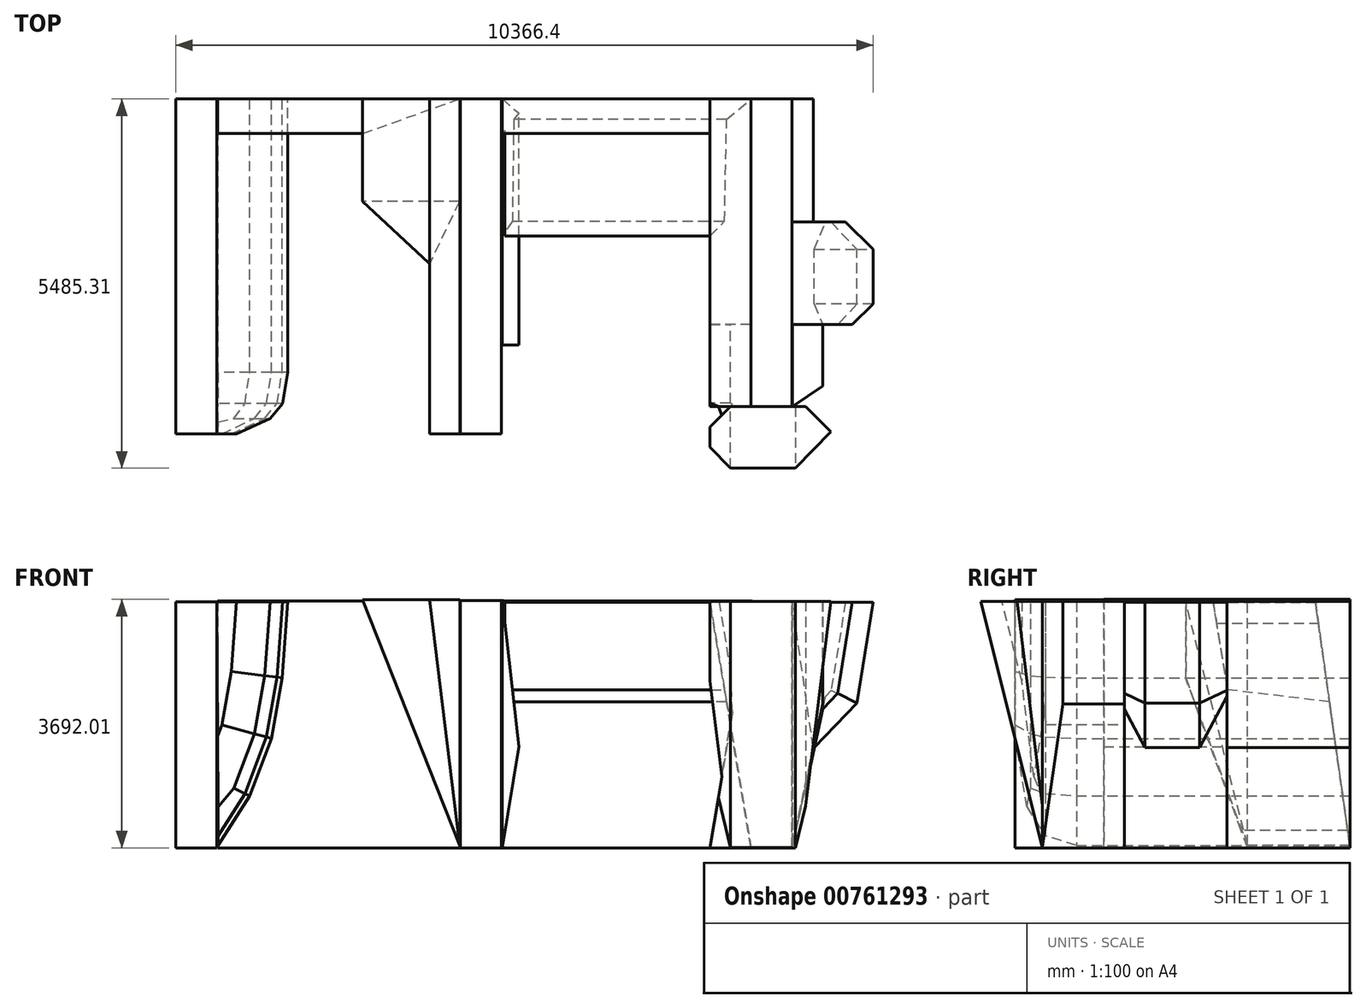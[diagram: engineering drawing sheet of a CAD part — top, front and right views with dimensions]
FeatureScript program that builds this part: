
annotation { "Feature Type Name" : "Feature", "Feature Type Description" : "" }
export const myFeature = defineFeature(function(context is Context, id is Id, definition is map)
    precondition{}
    {
        {
            var Q0;
            Q0=qCreatedBy(makeId("Front.planeOp"),FACE);
            var sketch = newSketch(context, id + "F0", { "sketchPlane" : qUnion([Q0])});
            skLineSegment(sketch, "E0.bottom", {"start": v(0, 0) * mm, "end": v(609.6, 0) * mm});
            skLineSegment(sketch, "E0.top", {"start": v(0, 3657.6) * mm, "end": v(609.6, 3657.6) * mm});
            skLineSegment(sketch, "E0.left", {"start": v(0, 0) * mm, "end": v(0, 3657.6) * mm});
            skLineSegment(sketch, "E0.right", {"start": v(609.6, 0) * mm, "end": v(609.6, 3657.6) * mm});
            skSolve(sketch);
        }
        {
            var Q0;
            Q0 = qSketchRegion(id + "F0", true);
            extrude(context, id + "F1", {"entities" : qUnion([Q0]), "depth" : 4572 * mm, "offsetDistance" : 25.4 * mm});
        }
        {
            var Q0;
            Q0=qCreatedBy(makeId("Front.planeOp"),FACE);
            var sketch = newSketch(context, id + "F2", { "sketchPlane" : qUnion([Q0])});
            skLineSegment(sketch, "E1", {"start": v(612.05, 0) * mm, "end": v(1069.66, 2135.93) * mm});
            skLineSegment(sketch, "E2", {"start": v(1069.66, 2135.93) * mm, "end": v(1069.66, 3659.93) * mm});
            skLineSegment(sketch, "E3", {"start": v(1069.66, 3659.93) * mm, "end": v(618.62, 3659.93) * mm});
            skLineSegment(sketch, "E4", {"start": v(618.62, 3659.93) * mm, "end": v(612.05, 0) * mm});
            skSolve(sketch);
        }
        {
            var Q0;
            Q0 = qSketchRegion(id + "F2", true);
            extrude(context, id + "F3", {"entities" : qUnion([Q0]), "depth" : 4572 * mm, "offsetDistance" : 25.4 * mm, "hasSecondDirection" : true, "secondDirectionOppositeDirection" : false, "secondDirectionDepth" : 3352.8 * mm});
        }
        {
            var Q0;
            Q0=makeQuery(id+"F3.opExtrude","CAP_EDGE",EDGE,{"disambiguationData":[OSD([sQuery(id+"F2.wireOp",EDGE,"E2")])],"isStart":false});
            chamfer(context, id + "F4", {"entities" : qUnion([Q0]), "chamferType" : ChamferType.TWO_OFFSETS, "width1" : 457.2 * mm, "oppositeDirection" : false, "width2" : 304.8 * mm, "tangentPropagation" : true});
        }
        {
            var Q0;
            Q0=qCreatedBy(makeId("Front.planeOp"),FACE);
            var sketch = newSketch(context, id + "F5", { "sketchPlane" : qUnion([Q0])});
            skLineSegment(sketch, "E5", {"start": v(618.5, 0) * mm, "end": v(942.34, 1489.2) * mm});
            skLineSegment(sketch, "E6", {"start": v(942.34, 1489.2) * mm, "end": v(1573.15, 2151.17) * mm});
            skLineSegment(sketch, "E7", {"start": v(1573.15, 2151.17) * mm, "end": v(1816.44, 3651.3) * mm});
            skLineSegment(sketch, "E8", {"start": v(1816.44, 3651.3) * mm, "end": v(1054.44, 3651.3) * mm});
            skLineSegment(sketch, "E9", {"start": v(1054.44, 3651.3) * mm, "end": v(611.92, 3651.3) * mm});
            skLineSegment(sketch, "E10", {"start": v(611.92, 3651.3) * mm, "end": v(618.5, 0) * mm});
            skSolve(sketch);
        }
        {
            var Q0;
            Q0 = qSketchRegion(id + "F5", true);
            extrude(context, id + "F6", {"entities" : qUnion([Q0]), "operationType" : NewBodyOperationType.ADD, "depth" : 3352.8 * mm, "offsetDistance" : 25.4 * mm, "hasSecondDirection" : true, "secondDirectionOppositeDirection" : true, "secondDirectionDepth" : -1828.8 * mm});
        }
        {
            var Q0;
            Q0=makeQuery(id+"F6.opExtrude","CAP_EDGE",EDGE,{"disambiguationData":[OSD([sQuery(id+"F5.wireOp",EDGE,"E7")])],"isStart":false});
            var Q1;
            Q1=makeQuery(id+"F6.opExtrude","CAP_EDGE",EDGE,{"disambiguationData":[OSD([sQuery(id+"F5.wireOp",EDGE,"E6")])],"isStart":false});
            chamfer(context, id + "F7", {"entities" : qUnion([Q0, Q1]), "width" : 304.8 * mm, "tangentPropagation" : true});
        }
        {
            var Q0;
            Q0=makeQuery(id+"F6.opExtrude","CAP_EDGE",EDGE,{"disambiguationData":[OSD([sQuery(id+"F5.wireOp",EDGE,"E7")])],"isStart":true});
            var Q1;
            Q1=makeQuery(id+"F6.opExtrude","CAP_EDGE",EDGE,{"disambiguationData":[OSD([sQuery(id+"F5.wireOp",EDGE,"E6")])],"isStart":true});
            chamfer(context, id + "F8", {"entities" : qUnion([Q0, Q1]), "width" : 406.4 * mm, "tangentPropagation" : true});
        }
        {
            var Q0;
            Q0=qCreatedBy(makeId("Front.planeOp"),FACE);
            var sketch = newSketch(context, id + "F9", { "sketchPlane" : qUnion([Q0])});
            skLineSegment(sketch, "E11", {"start": v(610.13, 0) * mm, "end": v(925.77, 1490.96) * mm});
            skLineSegment(sketch, "E12", {"start": v(925.77, 1490.96) * mm, "end": v(610.13, 3664.47) * mm});
            skLineSegment(sketch, "E13", {"start": v(610.13, 3664.47) * mm, "end": v(610.13, 0) * mm});
            skSolve(sketch);
        }
        {
            var Q0;
            Q0 = qSketchRegion(id + "F9", true);
            extrude(context, id + "F10", {"entities" : qUnion([Q0]), "operationType" : NewBodyOperationType.ADD, "depth" : 1828.8 * mm, "offsetDistance" : 25.4 * mm});
        }
        {
            var Q0;
            Q0=qCreatedBy(makeId("Right.planeOp"),FACE);
            var sketch = newSketch(context, id + "F11", { "sketchPlane" : qUnion([Q0])});
            skLineSegment(sketch, "E14", {"start": v(-4570.91, 0) * mm, "end": v(-4570.91, 3662.43) * mm});
            skLineSegment(sketch, "E15", {"start": v(-4570.91, 3662.43) * mm, "end": v(-5485.31, 3662.43) * mm});
            skLineSegment(sketch, "E16", {"start": v(-5485.31, 3662.43) * mm, "end": v(-4570.91, 0) * mm});
            skSolve(sketch);
        }
        {
            var Q0;
            Q0 = qSketchRegion(id + "F11", true);
            extrude(context, id + "F12", {"entities" : qUnion([Q0]), "operationType" : NewBodyOperationType.ADD, "depth" : 1219.2 * mm, "offsetDistance" : 25.4 * mm, "hasSecondDirection" : true, "secondDirectionOppositeDirection" : true, "secondDirectionDepth" : 609.6 * mm});
        }
        {
            var Q0;
            Q0=makeQuery(id+"F12.opExtrude","CAP_EDGE",EDGE,{"disambiguationData":[OSD([sQuery(id+"F11.wireOp",EDGE,"E16")])],"isStart":false});
            chamfer(context, id + "F13", {"entities" : qUnion([Q0]), "width" : 558.8 * mm, "tangentPropagation" : true});
        }
        {
            var Q0;
            Q0=makeQuery(id+"F12.opExtrude","CAP_EDGE",EDGE,{"disambiguationData":[OSD([sQuery(id+"F11.wireOp",EDGE,"E14")])],"isStart":false});
            chamfer(context, id + "F14", {"entities" : qUnion([Q0]), "width" : 406.4 * mm, "tangentPropagation" : true});
        }
        {
            var Q0;
            Q0=qCreatedBy(makeId("Front.planeOp"),FACE);
            var sketch = newSketch(context, id + "F15", { "sketchPlane" : qUnion([Q0])});
            skLineSegment(sketch, "E17", {"start": v(0, 0) * mm, "end": v(-612.45, 3669.02) * mm});
            skLineSegment(sketch, "E18", {"start": v(-612.45, 3669.02) * mm, "end": v(0, 3669.02) * mm});
            skLineSegment(sketch, "E19", {"start": v(0, 3669.02) * mm, "end": v(0, 0) * mm});
            skSolve(sketch);
        }
        {
            var Q0;
            Q0 = qSketchRegion(id + "F15", true);
            extrude(context, id + "F16", {"entities" : qUnion([Q0]), "operationType" : NewBodyOperationType.ADD, "depth" : 4572 * mm, "offsetDistance" : 25.4 * mm});
        }
        {
            var Q0;
            Q0=qCreatedBy(makeId("Front.planeOp"),FACE);
            var sketch = newSketch(context, id + "F17", { "sketchPlane" : qUnion([Q0])});
            skLineSegment(sketch, "E20", {"start": v(-608.76, 0) * mm, "end": v(0, 3686.78) * mm});
            skLineSegment(sketch, "E21", {"start": v(0, 3686.78) * mm, "end": v(0, 0) * mm});
            skLineSegment(sketch, "E22", {"start": v(0, 0) * mm, "end": v(-608.76, 0) * mm});
            skSolve(sketch);
        }
        {
            var Q0;
            Q0 = qSketchRegion(id + "F17", true);
            extrude(context, id + "F18", {"entities" : qUnion([Q0]), "operationType" : NewBodyOperationType.ADD, "depth" : 4572 * mm, "offsetDistance" : 25.4 * mm, "hasSecondDirection" : true, "secondDirectionOppositeDirection" : false, "secondDirectionDepth" : 3352.8 * mm});
        }
        {
            var Q0;
            Q0=makeQuery(id+"F12.opExtrude","CAP_EDGE",EDGE,{"disambiguationData":[OSD([sQuery(id+"F11.wireOp",EDGE,"E14")])],"isStart":true});
            chamfer(context, id + "F19", {"entities" : qUnion([Q0]), "width" : 304.8 * mm, "tangentPropagation" : true});
        }
        {
            var Q0;
            {var subQ0=sQuery(id+"F15.wireOp",EDGE,"E17");Q0=makeQuery(id+"F16.boolean.opBoolean","SPLIT",EDGE,{"disambiguationData":[topologyDisambiguationEdgeConnected([makeQuery(id+"F16.opExtrude","SWEPT_FACE",FACE,{"disambiguationData":[OSD([subQ0])]}),makeQuery(id+"F16.opExtrude","CAP_FACE",FACE,{"disambiguationData":[OSD([subQ0,sQuery(id+"F15.wireOp",EDGE,"E18"),sQuery(id+"F15.wireOp",EDGE,"E19")])],"isStart":false})])],"derivedFrom":makeQuery(id+"F16.opExtrude","CAP_EDGE",EDGE,{"disambiguationData":[OSD([subQ0])],"isStart":false})});}
            chamfer(context, id + "F20", {"entities" : qUnion([Q0]), "width" : 5.08 * mm, "tangentPropagation" : true});
        }
        {
            var Q0;
            {var subQ0=sQuery(id+"F15.wireOp",EDGE,"E17");var subQ1=makeQuery(id+"F16.opExtrude","CAP_FACE",FACE,{"disambiguationData":[OSD([subQ0,sQuery(id+"F15.wireOp",EDGE,"E18"),sQuery(id+"F15.wireOp",EDGE,"E19")])],"isStart":false});Q0=makeQuery(id+"F20.opChamfer","BLEND_EDGE",EDGE,{"blendedFrom":[makeQuery(id+"F16.boolean.opBoolean","SPLIT",EDGE,{"disambiguationData":[topologyDisambiguationEdgeConnected([makeQuery(id+"F16.opExtrude","SWEPT_FACE",FACE,{"disambiguationData":[OSD([subQ0])]}),subQ1])],"derivedFrom":makeQuery(id+"F16.opExtrude","CAP_EDGE",EDGE,{"disambiguationData":[OSD([subQ0])],"isStart":false})}),makeQuery(id+"F18.boolean.opBoolean","MERGE",FACE,{"derivedFrom":[makeQuery(id+"F16.boolean.opBoolean","SPLIT",FACE,{"derivedFrom":subQ1}),makeQuery(id+"F18.opExtrude","CAP_FACE",FACE,{"disambiguationData":[OSD([sQuery(id+"F17.wireOp",EDGE,"E20"),sQuery(id+"F17.wireOp",EDGE,"E21"),sQuery(id+"F17.wireOp",EDGE,"E22")])],"isStart":false})]})],"blendedInto":[makeQuery(id+"F18.boolean.opBoolean","MERGE",FACE,{"derivedFrom":[makeQuery(id+"F16.boolean.opBoolean","SPLIT",FACE,{"derivedFrom":subQ1}),makeQuery(id+"F18.opExtrude","CAP_FACE",FACE,{"disambiguationData":[OSD([sQuery(id+"F17.wireOp",EDGE,"E20"),sQuery(id+"F17.wireOp",EDGE,"E21"),sQuery(id+"F17.wireOp",EDGE,"E22")])],"isStart":false})]})]});}
            chamfer(context, id + "F21", {"entities" : qUnion([Q0]), "width" : 304.8 * mm, "tangentPropagation" : true});
        }
        {
            var Q0;
            Q0=makeQuery(id+"F12.opExtrude","CAP_EDGE",EDGE,{"disambiguationData":[OSD([sQuery(id+"F11.wireOp",EDGE,"E16")])],"isStart":true});
            chamfer(context, id + "F22", {"entities" : qUnion([Q0]), "width" : 304.8 * mm, "tangentPropagation" : true});
        }
        {
            var Q0;
            Q0=qCreatedBy(makeId("Right.planeOp"),FACE);
            var sketch = newSketch(context, id + "F23", { "sketchPlane" : qUnion([Q0])});
            skLineSegment(sketch, "E23", {"start": v(0, 0) * mm, "end": v(0, 2133.6) * mm});
            skLineSegment(sketch, "E24", {"start": v(0, 2133.6) * mm, "end": v(-1816.18, 2348.05) * mm});
            skLineSegment(sketch, "E25", {"start": v(-1816.18, 2348.05) * mm, "end": v(-2033.76, 3650.8) * mm});
            skLineSegment(sketch, "E26", {"start": v(-2033.76, 3650.8) * mm, "end": v(0, 3650.8) * mm});
            skLineSegment(sketch, "E27", {"start": v(0, 3650.8) * mm, "end": v(0, 2133.6) * mm});
            skSolve(sketch);
        }
        {
            var Q0;
            Q0 = qSketchRegion(id + "F23", true);
            extrude(context, id + "F24", {"entities" : qUnion([Q0]), "operationType" : NewBodyOperationType.ADD, "depth" : 0 * mm, "offsetDistance" : 25.4 * mm, "hasSecondDirection" : true, "secondDirectionOppositeDirection" : true, "secondDirectionDepth" : 3657.6 * mm});
        }
        {
            var Q0;
            Q0=qCreatedBy(makeId("Right.planeOp"),FACE);
            var sketch = newSketch(context, id + "F25", { "sketchPlane" : qUnion([Q0])});
            skLineSegment(sketch, "E28", {"start": v(0, 0) * mm, "end": v(-513.54, 3664.84) * mm});
            skLineSegment(sketch, "E29", {"start": v(-513.54, 3664.84) * mm, "end": v(0, 3664.84) * mm});
            skLineSegment(sketch, "E30", {"start": v(0, 3664.84) * mm, "end": v(0, 0) * mm});
            skSolve(sketch);
        }
        {
            var Q0;
            Q0 = qSketchRegion(id + "F25", true);
            extrude(context, id + "F26", {"entities" : qUnion([Q0]), "operationType" : NewBodyOperationType.ADD, "depth" : 0 * mm, "offsetDistance" : 25.4 * mm, "hasSecondDirection" : true, "secondDirectionOppositeDirection" : true, "secondDirectionDepth" : 7924.8 * mm});
        }
        {
            var Q0;
            Q0=qCreatedBy(makeId("Front.planeOp"),FACE);
            var sketch = newSketch(context, id + "F27", { "sketchPlane" : qUnion([Q0])});
            skLineSegment(sketch, "E31", {"start": v(-3707.19, 0) * mm, "end": v(-3707.19, 3675.3) * mm});
            skLineSegment(sketch, "E32", {"start": v(-3707.19, 3675.3) * mm, "end": v(-4316.79, 3675.3) * mm});
            skLineSegment(sketch, "E33", {"start": v(-4316.79, 3675.3) * mm, "end": v(-4316.79, 0) * mm});
            skLineSegment(sketch, "E34", {"start": v(-4316.79, 0) * mm, "end": v(-3707.19, 0) * mm});
            skSolve(sketch);
        }
        {
            var Q0;
            Q0 = qSketchRegion(id + "F27", true);
            extrude(context, id + "F28", {"entities" : qUnion([Q0]), "operationType" : NewBodyOperationType.ADD, "depth" : 4978.4 * mm, "offsetDistance" : 25.4 * mm});
        }
        {
            var Q0;
            Q0=qCreatedBy(makeId("Front.planeOp"),FACE);
            var sketch = newSketch(context, id + "F29", { "sketchPlane" : qUnion([Q0])});
            skLineSegment(sketch, "E35", {"start": v(-3697.5, 0) * mm, "end": v(-3449.53, 1503.7) * mm});
            skLineSegment(sketch, "E36", {"start": v(-3449.53, 1503.7) * mm, "end": v(-3697.5, 3692) * mm});
            skLineSegment(sketch, "E37", {"start": v(-3697.5, 3692) * mm, "end": v(-3697.5, 0) * mm});
            skSolve(sketch);
        }
        {
            var Q0;
            Q0 = qSketchRegion(id + "F29", true);
            extrude(context, id + "F30", {"entities" : qUnion([Q0]), "operationType" : NewBodyOperationType.ADD, "depth" : 3657.6 * mm, "offsetDistance" : 25.4 * mm});
        }
        {
            var Q0;
            Q0=qCreatedBy(makeId("Front.planeOp"),FACE);
            var sketch = newSketch(context, id + "F31", { "sketchPlane" : qUnion([Q0])});
            skLineSegment(sketch, "E38.bottom", {"start": v(-7940.32, 0) * mm, "end": v(-8549.92, 0) * mm});
            skLineSegment(sketch, "E38.top", {"start": v(-7940.32, 3657.6) * mm, "end": v(-8549.92, 3657.6) * mm});
            skLineSegment(sketch, "E38.left", {"start": v(-7940.32, 0) * mm, "end": v(-7940.32, 3657.6) * mm});
            skLineSegment(sketch, "E38.right", {"start": v(-8549.92, 0) * mm, "end": v(-8549.92, 3657.6) * mm});
            skSolve(sketch);
        }
        {
            var Q0;
            Q0 = qSketchRegion(id + "F31", true);
            extrude(context, id + "F32", {"entities" : qUnion([Q0]), "depth" : 4978.4 * mm, "offsetDistance" : 25.4 * mm});
        }
        {
            var Q0;
            Q0=qCreatedBy(makeId("Front.planeOp"),FACE);
            var sketch = newSketch(context, id + "F33", { "sketchPlane" : qUnion([Q0])});
            skLineSegment(sketch, "E39", {"start": v(-7940.37, 0) * mm, "end": v(-7449.74, 771.63) * mm});
            skLineSegment(sketch, "E40", {"start": v(-7449.74, 771.63) * mm, "end": v(-7124.69, 1626.3) * mm});
            skLineSegment(sketch, "E41", {"start": v(-7124.69, 1626.3) * mm, "end": v(-6967.28, 2527.05) * mm});
            skLineSegment(sketch, "E42", {"start": v(-6967.28, 2527.05) * mm, "end": v(-6881.82, 3654.62) * mm});
            skLineSegment(sketch, "E43", {"start": v(-6881.82, 3654.62) * mm, "end": v(-7940.37, 3654.62) * mm});
            skLineSegment(sketch, "E44", {"start": v(-7940.37, 3654.62) * mm, "end": v(-7917.36, 7.22) * mm});
            skSolve(sketch);
        }
        {
            var Q0;
            Q0 = qSketchRegion(id + "F33", true);
            extrude(context, id + "F34", {"entities" : qUnion([Q0]), "depth" : 4978.4 * mm, "offsetDistance" : 25.4 * mm});
        }
        {
            var Q0;
            Q0=makeQuery(id+"F34.opExtrude","CAP_EDGE",EDGE,{"disambiguationData":[OSD([sQuery(id+"F33.wireOp",EDGE,"E42")])],"isStart":false});
            var Q1;
            Q1=makeQuery(id+"F34.opExtrude","CAP_EDGE",EDGE,{"disambiguationData":[OSD([sQuery(id+"F33.wireOp",EDGE,"E41")])],"isStart":false});
            var Q2;
            Q2=makeQuery(id+"F34.opExtrude","CAP_EDGE",EDGE,{"disambiguationData":[OSD([sQuery(id+"F33.wireOp",EDGE,"E40")])],"isStart":false});
            var Q3;
            Q3=makeQuery(id+"F34.opExtrude","CAP_EDGE",EDGE,{"disambiguationData":[OSD([sQuery(id+"F33.wireOp",EDGE,"E39")])],"isStart":false});
            chamfer(context, id + "F35", {"entities" : qUnion([Q0, Q1, Q2, Q3]), "chamferType" : ChamferType.TWO_OFFSETS, "width1" : 152.4 * mm, "oppositeDirection" : false, "width2" : 914.4 * mm, "tangentPropagation" : true});
        }
        {
            var Q0;
            {var subQ0=sQuery(id+"F33.wireOp",EDGE,"E42");Q0=makeQuery(id+"F35.opChamfer","BLEND_EDGE",EDGE,{"blendedFrom":[makeQuery(id+"F34.opExtrude","CAP_EDGE",EDGE,{"disambiguationData":[OSD([subQ0])],"isStart":false}),makeQuery(id+"F34.opExtrude","CAP_FACE",FACE,{"disambiguationData":[OSD([sQuery(id+"F33.wireOp",EDGE,"E39"),sQuery(id+"F33.wireOp",EDGE,"E40"),sQuery(id+"F33.wireOp",EDGE,"E41"),subQ0,sQuery(id+"F33.wireOp",EDGE,"E43"),sQuery(id+"F33.wireOp",EDGE,"E44")])],"isStart":false})],"blendedInto":[makeQuery(id+"F34.opExtrude","CAP_FACE",FACE,{"disambiguationData":[OSD([sQuery(id+"F33.wireOp",EDGE,"E39"),sQuery(id+"F33.wireOp",EDGE,"E40"),sQuery(id+"F33.wireOp",EDGE,"E41"),subQ0,sQuery(id+"F33.wireOp",EDGE,"E43"),sQuery(id+"F33.wireOp",EDGE,"E44")])],"isStart":false})]});}
            var Q1;
            {var subQ0=sQuery(id+"F33.wireOp",EDGE,"E41");Q1=makeQuery(id+"F35.opChamfer","BLEND_EDGE",EDGE,{"blendedFrom":[makeQuery(id+"F34.opExtrude","CAP_EDGE",EDGE,{"disambiguationData":[OSD([subQ0])],"isStart":false}),makeQuery(id+"F34.opExtrude","CAP_FACE",FACE,{"disambiguationData":[OSD([sQuery(id+"F33.wireOp",EDGE,"E39"),sQuery(id+"F33.wireOp",EDGE,"E40"),subQ0,sQuery(id+"F33.wireOp",EDGE,"E42"),sQuery(id+"F33.wireOp",EDGE,"E43"),sQuery(id+"F33.wireOp",EDGE,"E44")])],"isStart":false})],"blendedInto":[makeQuery(id+"F34.opExtrude","CAP_FACE",FACE,{"disambiguationData":[OSD([sQuery(id+"F33.wireOp",EDGE,"E39"),sQuery(id+"F33.wireOp",EDGE,"E40"),subQ0,sQuery(id+"F33.wireOp",EDGE,"E42"),sQuery(id+"F33.wireOp",EDGE,"E43"),sQuery(id+"F33.wireOp",EDGE,"E44")])],"isStart":false})]});}
            var Q2;
            {var subQ0=sQuery(id+"F33.wireOp",EDGE,"E40");Q2=makeQuery(id+"F35.opChamfer","BLEND_EDGE",EDGE,{"blendedFrom":[makeQuery(id+"F34.opExtrude","CAP_EDGE",EDGE,{"disambiguationData":[OSD([subQ0])],"isStart":false}),makeQuery(id+"F34.opExtrude","CAP_FACE",FACE,{"disambiguationData":[OSD([sQuery(id+"F33.wireOp",EDGE,"E39"),subQ0,sQuery(id+"F33.wireOp",EDGE,"E41"),sQuery(id+"F33.wireOp",EDGE,"E42"),sQuery(id+"F33.wireOp",EDGE,"E43"),sQuery(id+"F33.wireOp",EDGE,"E44")])],"isStart":false})],"blendedInto":[makeQuery(id+"F34.opExtrude","CAP_FACE",FACE,{"disambiguationData":[OSD([sQuery(id+"F33.wireOp",EDGE,"E39"),subQ0,sQuery(id+"F33.wireOp",EDGE,"E41"),sQuery(id+"F33.wireOp",EDGE,"E42"),sQuery(id+"F33.wireOp",EDGE,"E43"),sQuery(id+"F33.wireOp",EDGE,"E44")])],"isStart":false})]});}
            var Q3;
            {var subQ0=sQuery(id+"F33.wireOp",EDGE,"E39");Q3=makeQuery(id+"F35.opChamfer","BLEND_EDGE",EDGE,{"blendedFrom":[makeQuery(id+"F34.opExtrude","CAP_EDGE",EDGE,{"disambiguationData":[OSD([subQ0])],"isStart":false}),makeQuery(id+"F34.opExtrude","CAP_FACE",FACE,{"disambiguationData":[OSD([subQ0,sQuery(id+"F33.wireOp",EDGE,"E40"),sQuery(id+"F33.wireOp",EDGE,"E41"),sQuery(id+"F33.wireOp",EDGE,"E42"),sQuery(id+"F33.wireOp",EDGE,"E43"),sQuery(id+"F33.wireOp",EDGE,"E44")])],"isStart":false})],"blendedInto":[makeQuery(id+"F34.opExtrude","CAP_FACE",FACE,{"disambiguationData":[OSD([subQ0,sQuery(id+"F33.wireOp",EDGE,"E40"),sQuery(id+"F33.wireOp",EDGE,"E41"),sQuery(id+"F33.wireOp",EDGE,"E42"),sQuery(id+"F33.wireOp",EDGE,"E43"),sQuery(id+"F33.wireOp",EDGE,"E44")])],"isStart":false})]});}
            chamfer(context, id + "F36", {"entities" : qUnion([Q0, Q1, Q2, Q3]), "chamferType" : ChamferType.TWO_OFFSETS, "width1" : 304.8 * mm, "oppositeDirection" : false, "width2" : 457.2 * mm, "tangentPropagation" : true});
        }
        {
            var Q0;
            {var subQ0=sQuery(id+"F33.wireOp",EDGE,"E42");var subQ1=makeQuery(id+"F34.opExtrude","CAP_FACE",FACE,{"disambiguationData":[OSD([sQuery(id+"F33.wireOp",EDGE,"E39"),sQuery(id+"F33.wireOp",EDGE,"E40"),sQuery(id+"F33.wireOp",EDGE,"E41"),subQ0,sQuery(id+"F33.wireOp",EDGE,"E43"),sQuery(id+"F33.wireOp",EDGE,"E44")])],"isStart":false});Q0=makeQuery(id+"F36.opChamfer","BLEND_EDGE",EDGE,{"blendedFrom":[makeQuery(id+"F35.opChamfer","BLEND_EDGE",EDGE,{"blendedFrom":[makeQuery(id+"F34.opExtrude","CAP_EDGE",EDGE,{"disambiguationData":[OSD([subQ0])],"isStart":false}),subQ1],"blendedInto":[subQ1]}),subQ1],"blendedInto":[subQ1]});}
            var Q1;
            {var subQ0=sQuery(id+"F33.wireOp",EDGE,"E41");var subQ1=makeQuery(id+"F34.opExtrude","CAP_FACE",FACE,{"disambiguationData":[OSD([sQuery(id+"F33.wireOp",EDGE,"E39"),sQuery(id+"F33.wireOp",EDGE,"E40"),subQ0,sQuery(id+"F33.wireOp",EDGE,"E42"),sQuery(id+"F33.wireOp",EDGE,"E43"),sQuery(id+"F33.wireOp",EDGE,"E44")])],"isStart":false});Q1=makeQuery(id+"F36.opChamfer","BLEND_EDGE",EDGE,{"blendedFrom":[makeQuery(id+"F35.opChamfer","BLEND_EDGE",EDGE,{"blendedFrom":[makeQuery(id+"F34.opExtrude","CAP_EDGE",EDGE,{"disambiguationData":[OSD([subQ0])],"isStart":false}),subQ1],"blendedInto":[subQ1]}),subQ1],"blendedInto":[subQ1]});}
            var Q2;
            {var subQ0=sQuery(id+"F33.wireOp",EDGE,"E40");var subQ1=makeQuery(id+"F34.opExtrude","CAP_FACE",FACE,{"disambiguationData":[OSD([sQuery(id+"F33.wireOp",EDGE,"E39"),subQ0,sQuery(id+"F33.wireOp",EDGE,"E41"),sQuery(id+"F33.wireOp",EDGE,"E42"),sQuery(id+"F33.wireOp",EDGE,"E43"),sQuery(id+"F33.wireOp",EDGE,"E44")])],"isStart":false});Q2=makeQuery(id+"F36.opChamfer","BLEND_EDGE",EDGE,{"blendedFrom":[makeQuery(id+"F35.opChamfer","BLEND_EDGE",EDGE,{"blendedFrom":[makeQuery(id+"F34.opExtrude","CAP_EDGE",EDGE,{"disambiguationData":[OSD([subQ0])],"isStart":false}),subQ1],"blendedInto":[subQ1]}),subQ1],"blendedInto":[subQ1]});}
            chamfer(context, id + "F37", {"entities" : qUnion([Q0, Q1, Q2]), "chamferType" : ChamferType.TWO_OFFSETS, "width1" : 304.8 * mm, "oppositeDirection" : false, "width2" : 304.8 * mm, "tangentPropagation" : true});
        }
        {
            var Q0;
            Q0=qCreatedBy(makeId("Front.planeOp"),FACE);
            var sketch = newSketch(context, id + "F38", { "sketchPlane" : qUnion([Q0])});
            skLineSegment(sketch, "E45", {"start": v(-4315.98, 0) * mm, "end": v(-5769.16, 3686.31) * mm});
            skLineSegment(sketch, "E46", {"start": v(-5769.16, 3686.31) * mm, "end": v(-4327.49, 3686.31) * mm});
            skLineSegment(sketch, "E47", {"start": v(-4327.49, 3686.31) * mm, "end": v(-4315.98, 0) * mm});
            skSolve(sketch);
        }
        {
            var Q0;
            Q0 = qSketchRegion(id + "F38", true);
            extrude(context, id + "F39", {"entities" : qUnion([Q0]), "operationType" : NewBodyOperationType.ADD, "depth" : 2438.4 * mm, "offsetDistance" : 25.4 * mm});
        }
        {
            var Q0;
            Q0=makeQuery(id+"F39.opExtrude","CAP_EDGE",EDGE,{"disambiguationData":[OSD([sQuery(id+"F38.wireOp",EDGE,"E45")])],"isStart":false});
            chamfer(context, id + "F40", {"entities" : qUnion([Q0]), "chamferType" : ChamferType.TWO_OFFSETS, "width1" : 914.4 * mm, "oppositeDirection" : false, "width2" : 914.4 * mm, "tangentPropagation" : true});
        }
        {
            var Q0;
            Q0=qCreatedBy(makeId("Front.planeOp"),FACE);
            var sketch = newSketch(context, id + "F41", { "sketchPlane" : qUnion([Q0])});
            skLineSegment(sketch, "E48", {"start": v(-4327.49, 0) * mm, "end": v(-4776.22, 3689.14) * mm});
            skLineSegment(sketch, "E49", {"start": v(-4776.22, 3689.14) * mm, "end": v(-4327.49, 3689.14) * mm});
            skLineSegment(sketch, "E50", {"start": v(-4327.49, 3689.14) * mm, "end": v(-4327.49, 0) * mm});
            skSolve(sketch);
        }
        {
            var Q0;
            Q0 = qSketchRegion(id + "F41", true);
            extrude(context, id + "F42", {"entities" : qUnion([Q0]), "operationType" : NewBodyOperationType.ADD, "depth" : 4978.4 * mm, "offsetDistance" : 25.4 * mm});
        }
    });
